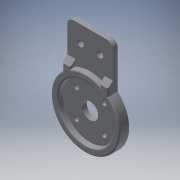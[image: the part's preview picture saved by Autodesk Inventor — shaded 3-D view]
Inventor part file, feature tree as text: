
AUTODESK INVENTOR PART (.ipt)
format: ipt  version: 2018 (Build 220112000, 112)  size: 218,112 bytes
history: native  units: in
note: dims shown in document units (in); Inventor stores cm internally (conversion verified against a paired STEP export)
features: extrude x4, sketch x4, projected_geometry x3, fillet x2, chamfer x1
ambient origin geometry x8: Origin, YZ Plane, XZ Plane, XY Plane, X Axis, Y Axis, Z Axis, Center Point
bodies: Solid1 (feature_tree)
feature tree (14):
  extrude  "Extrusion1"  Depth=1.7126in
  extrude  "Extrusion2"  Depth=1.1024in
  extrude  "Extrusion3"  Depth=0.7874in
  chamfer  "Chamfer1"  Distance=0.1969in
  fillet  "Fillet1"  Radius=0.1181in
  extrude  "Extrusion4"  Depth=0.3937in
  fillet  "Fillet2"  Radius=0.1654in
  sketch  "Sketch1"  dims[d0=1.6535in d1=1.7126in]
  sketch  "Sketch2"  dims[d2=0.1181in d3=0.0in d4=1.1024in]
  projected_geometry  "Projected Loop1"
  sketch  "Sketch3"  dims[d5=1.3189in d6=0.7874in]
  projected_geometry  "Projected Loop2"
  projected_geometry  "Projected Loop3"
  sketch  "Sketch4"  dims[d7=0.1969in d8=0.1969in d9=0.1181in d10=0.0in d11=0.3937in d12=0.1654in d13=0.4724in d14=0.3937in d15=0.1181in d16=0.0in d17=0.1181in d18=0.0787in d19=45.0deg d20=0.0394in d21=45.0deg d22=0.1299in d23=0.4724in d24=1.5748in d26=360.0deg d28=0.1181in d29=0.0in d30=0.1575in]
